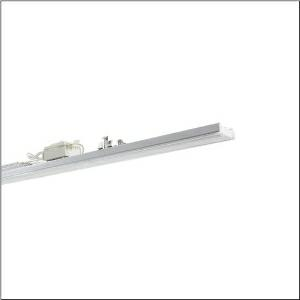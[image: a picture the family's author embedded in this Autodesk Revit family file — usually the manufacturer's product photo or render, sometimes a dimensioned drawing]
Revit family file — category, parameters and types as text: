
# Revit family: licross_11_recessed_ho_51tl11cn4c5s
name_source: partatom
category: Lighting Fixtures
units: mm (PartAtom-declared; Revit-internal decimal feet)

## family parameters
Cut with Voids When Loaded = No
Host = Face
Light Source = No
Part Type = Normal
Room Calculation Point = No
Round Connector Dimension = Use Diameter
Shared = No

## types (1)
- --- (1 x LED, 12710 lm, 66.5 W, 4000K)
    Apparent Load = 67 VA
    CIE Flux Codes = 87 95 99 100 100
    Color Rendering = 80
    Color Temperature = 4000K
    Default Elevation = 1800 mm
    Description = Licross 11 Recessed HO, luminaire insert, of sheet steel, coil coated, white, length: 1.500mm, width: 66mm, height: 67mm, LED rated luminous flux: 12.710lm, light colour: 840, SDCM (Standard Deviation of Colour Matching)MacAdam ≤ 2 SDCM (initial), control gear: ON/OFF Multilumen, CLOi, with plug, 3-pole, with phase selection, mains connection: 220..240V, AC, 50/60Hz, start of lifetime: 67W, end of service life: 75W, internal wiring halogen-free, primary light control with lens, of plastic, primary optical cover: cover, of PMMA, light emission: direct distribution, primary light characteristic: symmetric, protection rating (complete): IP40, insulation class (complete): insulation class I (protective earthing), certification: CE, ENEC, VDE, UKCA, protection symbol: D if used in an environment without relevant dust loads with corresponding accessories, impact resistance: IK06, permissible ambient temperature for indoor applications: -35..+35°C, corresponds to IFS (International Featured Standards) requirements for safety and quality in the food industry, reducing of maximum allowable ambient temperature of 5°C with ceiling mounting, LABS conformity tested according to VDMA 24364:2018-05, The light source and the operating device comply with the requirements of the Ecodesign Regulation (EU) 2019/2020 and are replaceable in accordance with this regulation, packaging unit: 1 piece
    Height = 58 mm
    Lamp = 1 x LED
    Lamp Light Flux = 12710 lm
    Lamp Power = 66.5 W
    Lamp count = 1
    Length = 1500 mm
    Luminous efficacy = 191 lm/W
    Manufacturer = Siteco
    ModVariant = No
    Model = 51TL11CN4C5S
    Mounting Place = Ceiling
    Mounting Type = Pendant
    Number of Poles = 1
    OnlyDefault = Yes
    Power Factor = 1
    Product Name = Licross 11 Recessed HO
    Product group = luminaire insert | ceiling pendant
    ProductGroupID = 901
    Protection Class = Protection class I
    Protection Degree = IP 40
    RLX_Detail_Level = 1
    RLX_Emergency_Light_Flux = 0 lm
    RLX_Emergency_Type = 0
    RLX_Emergency_Type_DB = No
    RlxData = <blob elided: 22557 chars, md5=7a71a038>
    Socket = socket
    Standby Power = 0 W
    System Light Flux = 12710 lm
    System Power = 67 W
    Type Comments = factory setting: luminous flux: 100 % | (A | C | E) | 156 mA
    Type Image = l_1296930.jpg
    URL = http://relux.com
    VarID = @adj_089879
    Voltage = 0 V
    Weight = 0.00 kg
    Width = 66 mm

## geometry (parser evidence)
native form markers: Blend x4, Sweep x11
no freeform markers — native parametric forms only
